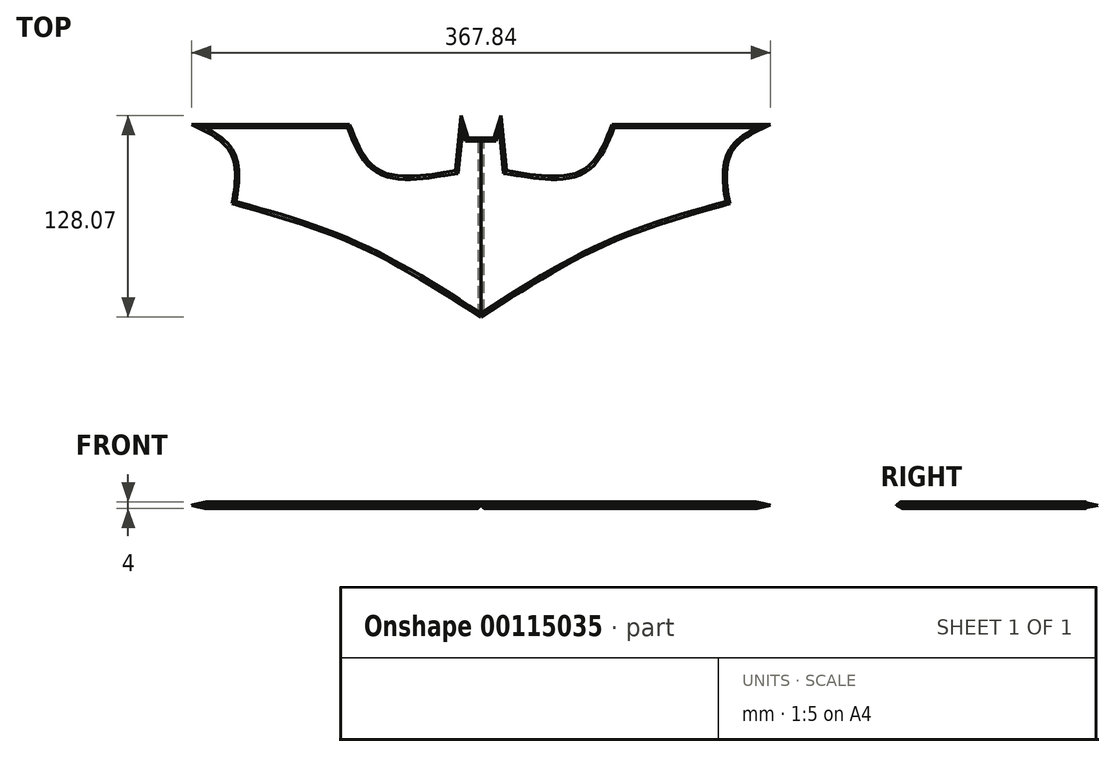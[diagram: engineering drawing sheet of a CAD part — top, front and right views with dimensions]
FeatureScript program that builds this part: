
annotation { "Feature Type Name" : "Feature", "Feature Type Description" : "" }
export const myFeature = defineFeature(function(context is Context, id is Id, definition is map)
    precondition{}
    {
        {
            var Q0;
            Q0=qCreatedBy(makeId("Top.planeOp"),FACE);
            var sketch = newSketch(context, id + "F0", { "sketchPlane" : qUnion([Q0])});
            skPoint(sketch, "E0.start.orphan", {"position": v(0, 39.19) * mm});
            skLineSegment(sketch, "E1", {"start": v(0, 39.19) * mm, "end": v(-8.2, 39.19) * mm});
            skLineSegment(sketch, "E2", {"start": v(-8.2, 39.19) * mm, "end": v(-12.73, 53.55) * mm});
            skLineSegment(sketch, "E3", {"start": v(-12.73, 53.55) * mm, "end": v(-16.25, 18.52) * mm});
            skLineSegment(sketch, "E4", {"start": v(0, 18.52) * mm, "end": v(0, 39.19) * mm});
            skFitSpline(sketch, "E5", {"points": [v(-16.25, 18.52) * mm, v(-64.13, 18.52) * mm, v(-83.29, 47.75) * mm], "startDerivative": vector(-101.52, -17.1) * mm, "endDerivative": vector(-30.7, 78.06) * mm});
            skLineSegment(sketch, "E6", {"start": v(-83.29, 47.75) * mm, "end": v(-183.92, 47.75) * mm});
            skFitSpline(sketch, "E7", {"points": [v(-183.92, 47.75) * mm, v(-156.93, 24.54) * mm, v(-158.2, -2.76) * mm, v(-158.2, -2.45) * mm], "startDerivative": vector(70.26, -31.93) * mm, "endDerivative": vector(0.87, 10.52) * mm});
            skFitSpline(sketch, "E8", {"points": [v(-158.2, -2.45) * mm, v(-78.5, -29.12) * mm, v(0, -74.52) * mm], "startDerivative": vector(164.54, -45.86) * mm, "endDerivative": vector(151.94, -97.96) * mm});
            skLineSegment(sketch, "E9", {"start": v(0, -74.52) * mm, "end": v(0, 39.19) * mm});
            skSolve(sketch);
        }
        {
            var Q0;
            Q0 = qSketchRegion(id + "F0", true);
            extrude(context, id + "F1", {"entities" : qUnion([Q0]), "depth" : 4 * mm});
        }
        {
            var Q0;
            Q0=makeQuery(id+"F1.opExtrude","SWEPT_BODY",BODY,{"disambiguationData":[OSD([sQuery(id+"F0.wireOp",EDGE,"E1"),sQuery(id+"F0.wireOp",EDGE,"E2"),sQuery(id+"F0.wireOp",EDGE,"E3"),sQuery(id+"F0.wireOp",EDGE,"E5"),sQuery(id+"F0.wireOp",EDGE,"E6"),sQuery(id+"F0.wireOp",EDGE,"E7"),sQuery(id+"F0.wireOp",EDGE,"E8"),sQuery(id+"F0.wireOp",EDGE,"E9")])]});
            var Q1;
            Q1=qCreatedBy(makeId("Right.planeOp"),FACE);
            mirror(context, id + "F2", {"operationType" : NewBodyOperationType.ADD, "entities" : qUnion([Q0]), "mirrorPlane" : qUnion([Q1])});
        }
        {
            var Q0;
            Q0=makeQuery(id+"F1.opExtrude","SWEPT_BODY",BODY,{"disambiguationData":[OSD([sQuery(id+"F0.wireOp",EDGE,"E7"),sQuery(id+"F0.wireOp",EDGE,"E8")])]});
            deleteBodies(context, id + "F3", {"entities" : qUnion([Q0])});
        }
        {
            var Q0;
            {var subQ0=sQuery(id+"F0.wireOp",EDGE,"E8");Q0=makeQuery(id+"F1.opExtrude","CAP_EDGE",EDGE,{"disambiguationData":[OSD([subQ0]),TDD([makeQuery(id+"F0.imprint","IMPRINT",EDGE,{"disambiguationData":[TD([[makeQuery(id+"F0.imprint","INTERSECT",VERTEX,{"derivedFrom":[subQ0,sQuery(id+"F0.wireOp",EDGE,"E9")]}),1.0]])],"derivedFrom":subQ0})])],"isStart":false});}
            var Q1;
            {var subQ0=sQuery(id+"F0.wireOp",EDGE,"E7");Q1=makeQuery(id+"F1.opExtrude","CAP_EDGE",EDGE,{"disambiguationData":[OSD([subQ0]),TDD([makeQuery(id+"F0.imprint","IMPRINT",EDGE,{"disambiguationData":[TD([[makeQuery(id+"F0.imprint","INTERSECT",VERTEX,{"derivedFrom":[sQuery(id+"F0.wireOp",EDGE,"E6"),subQ0]}),-1.0]])],"derivedFrom":subQ0})])],"isStart":false});}
            var Q2;
            Q2=makeQuery(id+"F1.opExtrude","CAP_EDGE",EDGE,{"disambiguationData":[OSD([sQuery(id+"F0.wireOp",EDGE,"E5")])],"isStart":false});
            var Q3;
            Q3=makeQuery(id+"F1.opExtrude","CAP_EDGE",EDGE,{"disambiguationData":[OSD([sQuery(id+"F0.wireOp",EDGE,"E6")])],"isStart":false});
            var Q4;
            Q4=makeQuery(id+"F1.opExtrude","CAP_EDGE",EDGE,{"disambiguationData":[OSD([sQuery(id+"F0.wireOp",EDGE,"E3")])],"isStart":false});
            var Q5;
            {var subQ0=makeQuery(id+"F1.opExtrude","CAP_EDGE",EDGE,{"disambiguationData":[OSD([sQuery(id+"F0.wireOp",EDGE,"E1")])],"isStart":false});Q5=makeQuery(id+"F2.boolean.opBoolean","MERGE",EDGE,{"derivedFrom":[subQ0,makeQuery(id+"F2.opPattern","COPY",EDGE,{"derivedFrom":subQ0,"instanceName":"1"})]});}
            var Q6;
            Q6=makeQuery(id+"F1.opExtrude","CAP_EDGE",EDGE,{"disambiguationData":[OSD([sQuery(id+"F0.wireOp",EDGE,"E2")])],"isStart":false});
            var Q7;
            Q7=makeQuery(id+"F2.opPattern","COPY",EDGE,{"derivedFrom":makeQuery(id+"F1.opExtrude","CAP_EDGE",EDGE,{"disambiguationData":[OSD([sQuery(id+"F0.wireOp",EDGE,"E2")])],"isStart":false}),"instanceName":"1"});
            var Q8;
            Q8=makeQuery(id+"F2.opPattern","COPY",EDGE,{"derivedFrom":makeQuery(id+"F1.opExtrude","CAP_EDGE",EDGE,{"disambiguationData":[OSD([sQuery(id+"F0.wireOp",EDGE,"E3")])],"isStart":false}),"instanceName":"1"});
            var Q9;
            Q9=makeQuery(id+"F2.opPattern","COPY",EDGE,{"derivedFrom":makeQuery(id+"F1.opExtrude","CAP_EDGE",EDGE,{"disambiguationData":[OSD([sQuery(id+"F0.wireOp",EDGE,"E5")])],"isStart":false}),"instanceName":"1"});
            var Q10;
            Q10=makeQuery(id+"F2.opPattern","COPY",EDGE,{"derivedFrom":makeQuery(id+"F1.opExtrude","CAP_EDGE",EDGE,{"disambiguationData":[OSD([sQuery(id+"F0.wireOp",EDGE,"E6")])],"isStart":false}),"instanceName":"1"});
            var Q11;
            {var subQ0=sQuery(id+"F0.wireOp",EDGE,"E7");Q11=makeQuery(id+"F2.opPattern","COPY",EDGE,{"derivedFrom":makeQuery(id+"F1.opExtrude","CAP_EDGE",EDGE,{"disambiguationData":[OSD([subQ0]),TDD([makeQuery(id+"F0.imprint","IMPRINT",EDGE,{"disambiguationData":[TD([[makeQuery(id+"F0.imprint","INTERSECT",VERTEX,{"derivedFrom":[sQuery(id+"F0.wireOp",EDGE,"E6"),subQ0]}),-1.0]])],"derivedFrom":subQ0})])],"isStart":false}),"instanceName":"1"});}
            var Q12;
            {var subQ0=sQuery(id+"F0.wireOp",EDGE,"E8");Q12=makeQuery(id+"F2.opPattern","COPY",EDGE,{"derivedFrom":makeQuery(id+"F1.opExtrude","CAP_EDGE",EDGE,{"disambiguationData":[OSD([subQ0]),TDD([makeQuery(id+"F0.imprint","IMPRINT",EDGE,{"disambiguationData":[TD([[makeQuery(id+"F0.imprint","INTERSECT",VERTEX,{"derivedFrom":[subQ0,sQuery(id+"F0.wireOp",EDGE,"E9")]}),1.0]])],"derivedFrom":subQ0})])],"isStart":false}),"instanceName":"1"});}
            chamfer(context, id + "F4", {"entities" : qUnion([Q0, Q1, Q2, Q3, Q4, Q5, Q6, Q7, Q8, Q9, Q10, Q11, Q12]), "width" : 2 * mm, "tangentPropagation" : true});
        }
        {
            var Q0;
            {var subQ0=makeQuery(id+"F1.opExtrude","CAP_FACE",FACE,{"disambiguationData":[OSD([sQuery(id+"F0.wireOp",EDGE,"E1"),sQuery(id+"F0.wireOp",EDGE,"E2"),sQuery(id+"F0.wireOp",EDGE,"E3"),sQuery(id+"F0.wireOp",EDGE,"E5"),sQuery(id+"F0.wireOp",EDGE,"E6"),sQuery(id+"F0.wireOp",EDGE,"E7"),sQuery(id+"F0.wireOp",EDGE,"E8"),sQuery(id+"F0.wireOp",EDGE,"E9")])],"isStart":true});Q0=makeQuery(id+"F2.boolean.opBoolean","MERGE",FACE,{"derivedFrom":[subQ0,makeQuery(id+"F2.opPattern","COPY",FACE,{"derivedFrom":subQ0,"instanceName":"1"})]});}
            chamfer(context, id + "F5", {"entities" : qUnion([Q0]), "width" : 2 * mm, "tangentPropagation" : true});
        }
    });
